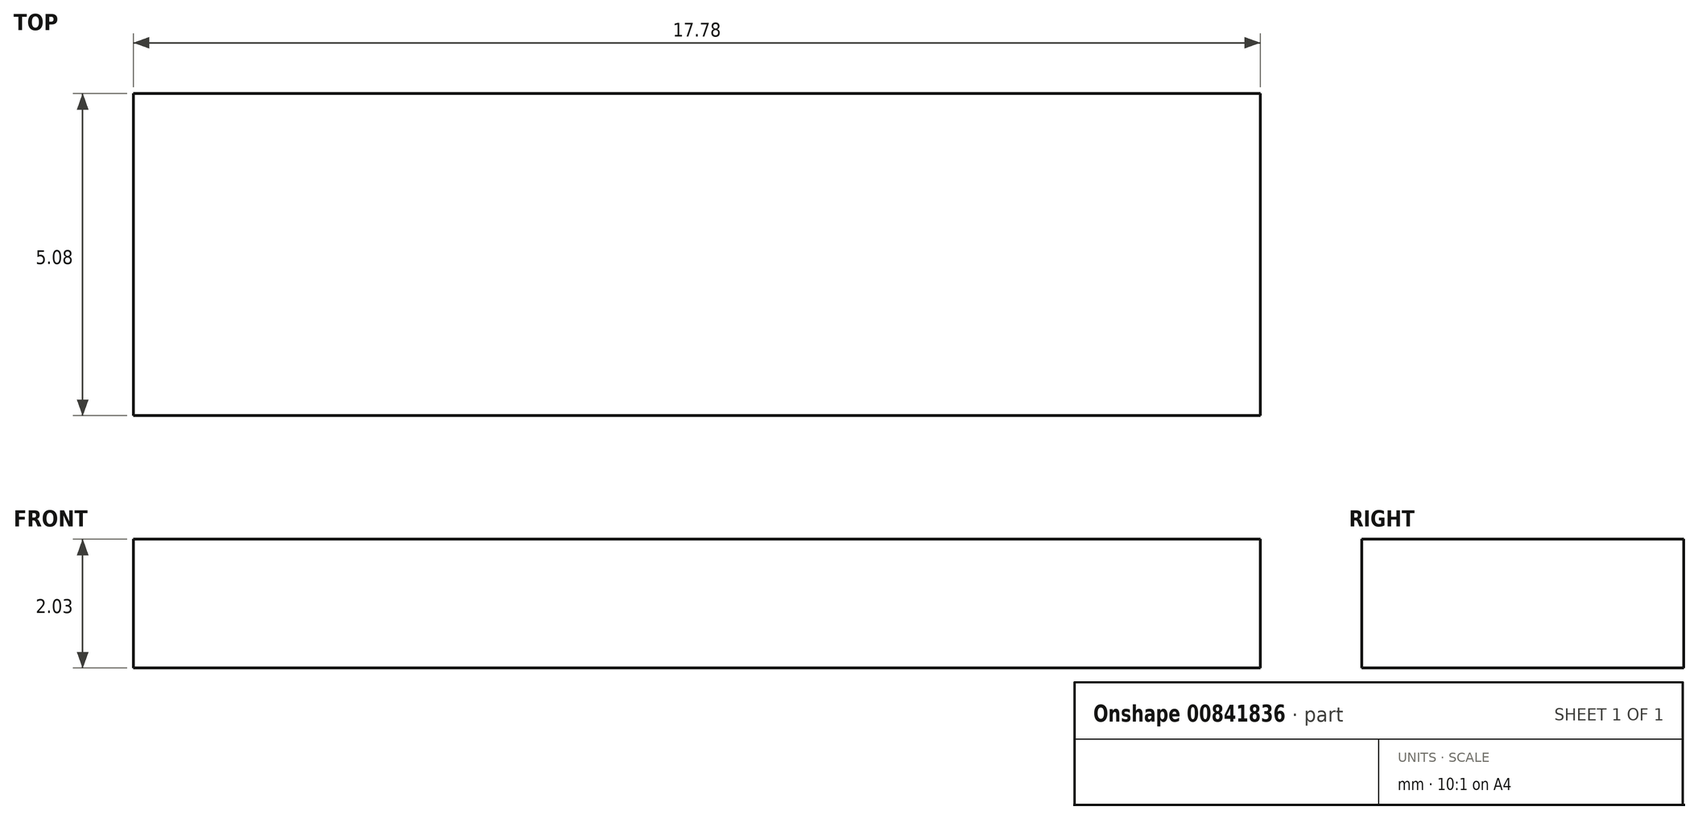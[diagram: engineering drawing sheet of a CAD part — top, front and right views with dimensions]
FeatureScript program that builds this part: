
annotation { "Feature Type Name" : "Feature", "Feature Type Description" : "" }
export const myFeature = defineFeature(function(context is Context, id is Id, definition is map)
    precondition{}
    {
        {
            var Q0;
            Q0=qCreatedBy(makeId("Top.planeOp"),FACE);
            var sketch = newSketch(context, id + "F0", { "sketchPlane" : qUnion([Q0])});
            skLineSegment(sketch, "E0.bottom", {"start": v(8.9, -2.54) * mm, "end": v(-8.9, -2.54) * mm});
            skLineSegment(sketch, "E0.top", {"start": v(8.9, 2.54) * mm, "end": v(-8.9, 2.54) * mm});
            skLineSegment(sketch, "E0.left", {"start": v(8.9, -2.54) * mm, "end": v(8.9, 2.54) * mm});
            skLineSegment(sketch, "E0.right", {"start": v(-8.9, -2.54) * mm, "end": v(-8.9, 2.54) * mm});
            skPoint(sketch, "E0.middle", {"position": v(0, 0) * mm});
            skSolve(sketch);
        }
        {
            var Q0;
            Q0 = qSketchRegion(id + "F0", true);
            extrude(context, id + "F1", {"entities" : qUnion([Q0]), "depth" : 2.03 * mm, "offsetDistance" : 25.4 * mm});
        }
    });
